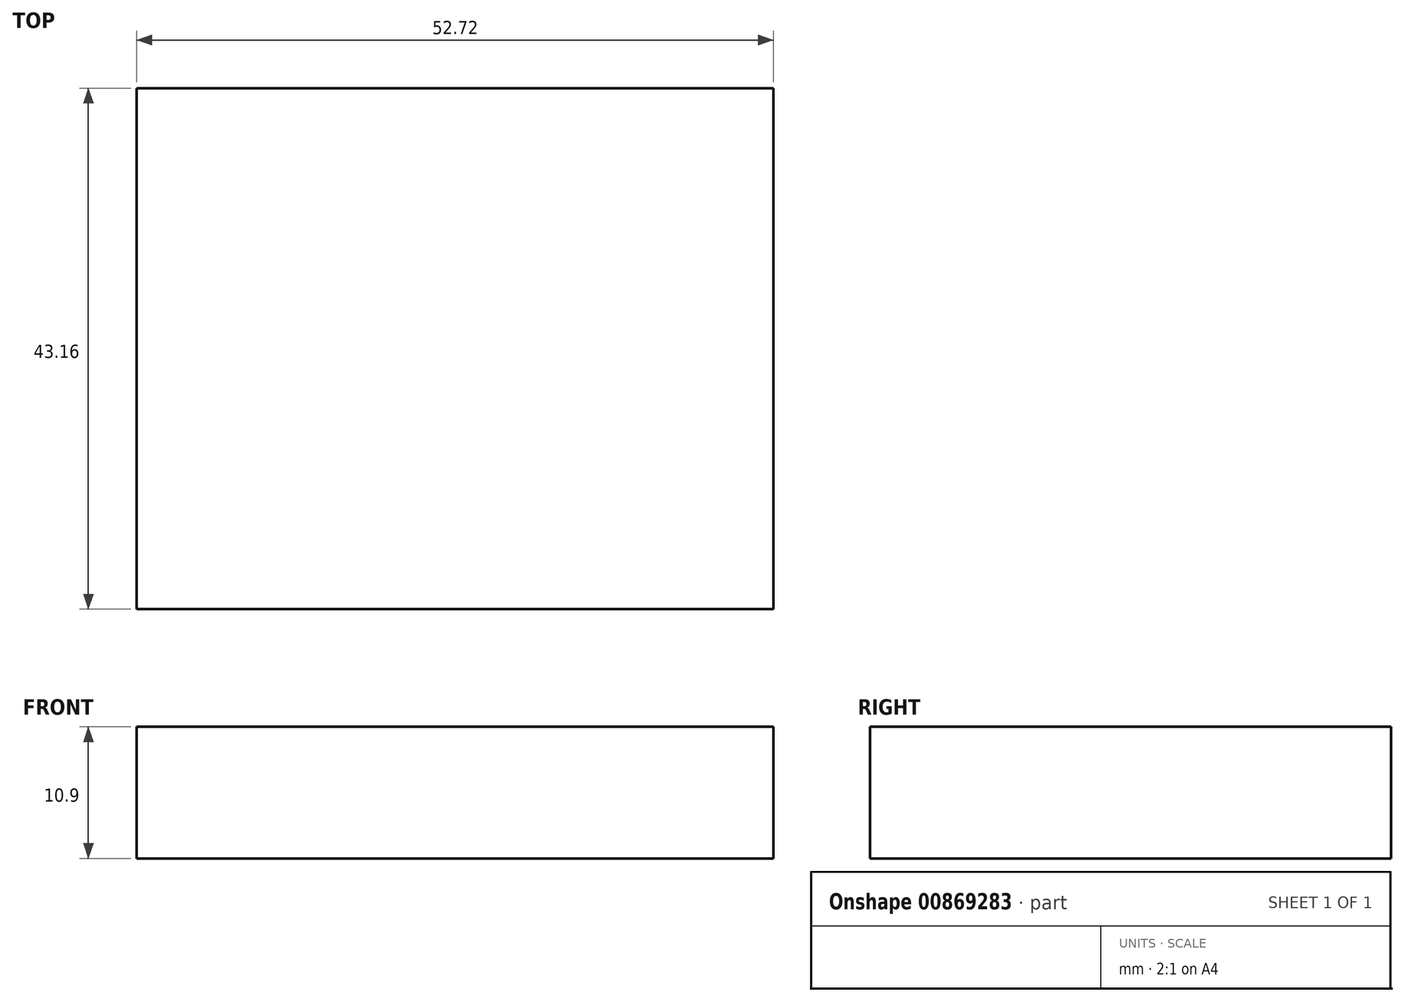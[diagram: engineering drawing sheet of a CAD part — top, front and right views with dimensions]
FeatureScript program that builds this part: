
annotation { "Feature Type Name" : "Feature", "Feature Type Description" : "" }
export const myFeature = defineFeature(function(context is Context, id is Id, definition is map)
    precondition{}
    {
        {
            var Q0;
            Q0=qCreatedBy(makeId("Top.planeOp"),FACE);
            var sketch = newSketch(context, id + "F0", { "sketchPlane" : qUnion([Q0])});
            skLineSegment(sketch, "E0.bottom", {"start": v(-40.62, 0) * mm, "end": v(12.1, 0) * mm});
            skLineSegment(sketch, "E0.top", {"start": v(-40.62, 43.16) * mm, "end": v(12.1, 43.16) * mm});
            skLineSegment(sketch, "E0.left", {"start": v(-40.62, 0) * mm, "end": v(-40.62, 43.16) * mm});
            skLineSegment(sketch, "E0.right", {"start": v(12.1, 0) * mm, "end": v(12.1, 43.16) * mm});
            skSolve(sketch);
        }
        {
            var Q0;
            Q0 = qSketchRegion(id + "F0", true);
            extrude(context, id + "F1", {"entities" : qUnion([Q0]), "depth" : 10.9 * mm, "offsetDistance" : 25 * mm});
        }
    });
